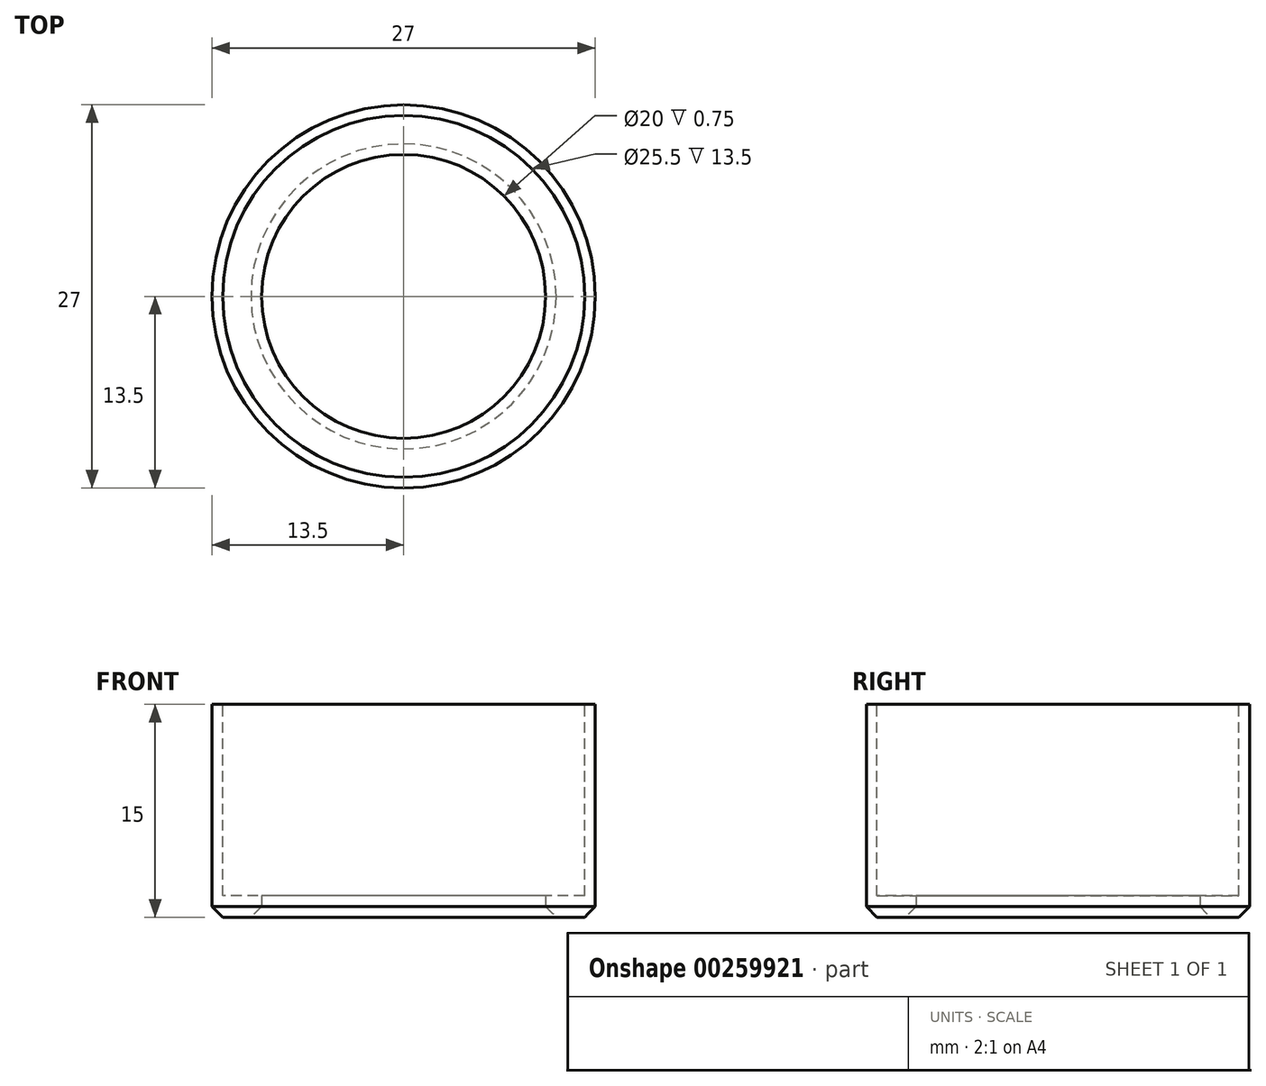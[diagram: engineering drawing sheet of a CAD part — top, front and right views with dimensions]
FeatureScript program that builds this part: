
annotation { "Feature Type Name" : "Feature", "Feature Type Description" : "" }
export const myFeature = defineFeature(function(context is Context, id is Id, definition is map)
    precondition{}
    {
        {
            var Q0;
            Q0=qCreatedBy(makeId("Top.planeOp"),FACE);
            var sketch = newSketch(context, id + "F0", { "sketchPlane" : qUnion([Q0])});
            skCircle(sketch, "E0", {"center": v(0, 0) * mm, "radius": 13.5 * mm});
            skCircle(sketch, "E1", {"center": v(0, 0) * mm, "radius": 10 * mm});
            skSolve(sketch);
        }
        {
            var Q0;
            Q0 = qSketchRegion(id + "F0", true);
            extrude(context, id + "F1", {"entities" : qUnion([Q0]), "depth" : 15 * mm});
        }
        {
            var Q0;
            Q0=makeQuery(id+"F1.opExtrude","CAP_FACE",FACE,{"disambiguationData":[OSD([sQuery(id+"F0.wireOp",EDGE,"E0"),sQuery(id+"F0.wireOp",EDGE,"E1")])],"isStart":false});
            var sketch = newSketch(context, id + "F2", { "sketchPlane" : qUnion([Q0])});
            skCircle(sketch, "E2", {"center": v(0, 0) * mm, "radius": 12.75 * mm});
            skSolve(sketch);
        }
        {
            var Q0;
            Q0 = qSketchRegion(id + "F2", true);
            extrude(context, id + "F3", {"entities" : qUnion([Q0]), "operationType" : NewBodyOperationType.REMOVE, "oppositeDirection" : true, "depth" : 13.5 * mm});
        }
        {
            var Q0;
            Q0=makeQuery(id+"F1.opExtrude","CAP_FACE",FACE,{"disambiguationData":[OSD([sQuery(id+"F0.wireOp",EDGE,"E0"),sQuery(id+"F0.wireOp",EDGE,"E1")])],"isStart":true});
            chamfer(context, id + "F4", {"entities" : qUnion([Q0]), "width" : .75 * mm, "tangentPropagation" : true});
        }
    });
